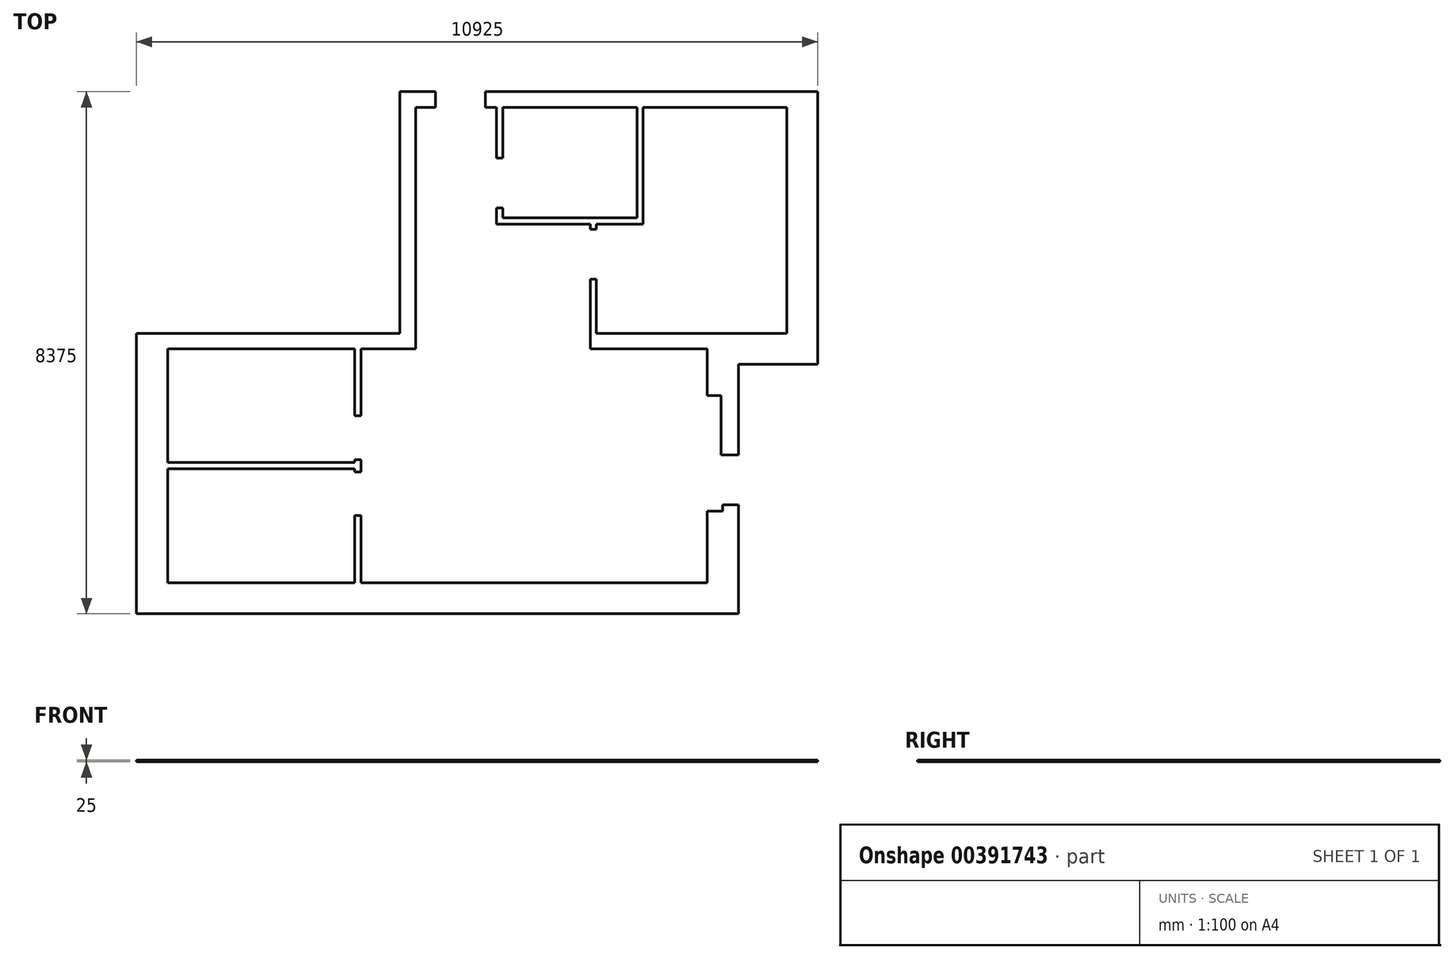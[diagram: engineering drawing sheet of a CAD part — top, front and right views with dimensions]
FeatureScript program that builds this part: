
annotation { "Feature Type Name" : "Feature", "Feature Type Description" : "" }
export const myFeature = defineFeature(function(context is Context, id is Id, definition is map)
    precondition{}
    {
        {
            var Q0;
            Q0=qCreatedBy(makeId("Top.planeOp"),FACE);
            var sketch = newSketch(context, id + "F0", { "sketchPlane" : qUnion([Q0])});
            skLineSegment(sketch, "E0.bottom", {"start": v(0, 0) * mm, "end": v(9650, 0) * mm});
            skLineSegment(sketch, "E0.top", {"start": v(4225, 8375) * mm, "end": v(4795, 8375) * mm});
            skLineSegment(sketch, "E0.left", {"start": v(0, 0) * mm, "end": v(0, 4500) * mm});
            skLineSegment(sketch, "E0.right", {"start": v(9650, 0) * mm, "end": v(9650, 1750) * mm});
            skLineSegment(sketch, "E1.bottom", {"start": v(500, 500) * mm, "end": v(3500, 500) * mm});
            skLineSegment(sketch, "E1.top", {"start": v(500, 4250) * mm, "end": v(3500, 4250) * mm});
            skLineSegment(sketch, "E1.left", {"start": v(500, 500) * mm, "end": v(500, 2325) * mm});
            skLineSegment(sketch, "E1.right", {"start": v(3500, 500) * mm, "end": v(3500, 1575) * mm});
            skLineSegment(sketch, "E2.bottom", {"start": v(3600, 4250) * mm, "end": v(4775, 4250) * mm});
            skLineSegment(sketch, "E2.top", {"start": v(3600, 500) * mm, "end": v(9150, 500) * mm});
            skLineSegment(sketch, "E2.left", {"start": v(3600, 4250) * mm, "end": v(3600, 3175) * mm});
            skLineSegment(sketch, "E2.right", {"start": v(9150, 4250) * mm, "end": v(9150, 3500) * mm});
            skLineSegment(sketch, "E3.bottom", {"start": v(10425, 4500) * mm, "end": v(7375, 4500) * mm});
            skLineSegment(sketch, "E3.left", {"start": v(10425, 4500) * mm, "end": v(10425, 8125) * mm});
            skLineSegment(sketch, "E3.right", {"start": v(7375, 4500) * mm, "end": v(7375, 5370) * mm});
            skLineSegment(sketch, "E4.top", {"start": v(4475, 8125) * mm, "end": v(4795, 8125) * mm});
            skLineSegment(sketch, "E4.left", {"start": v(4475, 4500) * mm, "end": v(4475, 8125) * mm});
            skLineSegment(sketch, "E5.bottom", {"start": v(7275, 4500) * mm, "end": v(5575, 4500) * mm});
            skLineSegment(sketch, "E5.top", {"start": v(7275, 6250) * mm, "end": v(5775, 6250) * mm});
            skLineSegment(sketch, "E5.left", {"start": v(7275, 4500) * mm, "end": v(7275, 5370) * mm});
            skLineSegment(sketch, "E6.top", {"start": v(10425, 8125) * mm, "end": v(8125, 8125) * mm});
            skLineSegment(sketch, "E6.right", {"start": v(5875, 6350) * mm, "end": v(5875, 6510) * mm});
            skLineSegment(sketch, "E7.trimOffspring", {"start": v(5775, 6250) * mm, "end": v(5775, 6510) * mm});
            skLineSegment(sketch, "E8", {"start": v(0, 4500) * mm, "end": v(4225, 4500) * mm});
            skLineSegment(sketch, "E9", {"start": v(4225, 4500) * mm, "end": v(4225, 8375) * mm});
            skLineSegment(sketch, "E10", {"start": v(500, 2325) * mm, "end": v(3500, 2325) * mm});
            skLineSegment(sketch, "E11", {"start": v(500, 2425) * mm, "end": v(3500, 2425) * mm});
            skLineSegment(sketch, "E12.trimOffspring", {"start": v(3500, 2425) * mm, "end": v(3500, 2475) * mm});
            skLineSegment(sketch, "E13.trimOffspring", {"start": v(500, 2425) * mm, "end": v(500, 4250) * mm});
            skLineSegment(sketch, "E14", {"start": v(9650, 4000) * mm, "end": v(10925, 4000) * mm});
            skLineSegment(sketch, "E15", {"start": v(10925, 4000) * mm, "end": v(10925, 8375) * mm});
            skLineSegment(sketch, "E16", {"start": v(3500, 2275) * mm, "end": v(3600, 2275) * mm});
            skLineSegment(sketch, "E17", {"start": v(3500, 1575) * mm, "end": v(3600, 1575) * mm});
            skLineSegment(sketch, "E18", {"start": v(3500, 2475) * mm, "end": v(3600, 2475) * mm});
            skLineSegment(sketch, "E19", {"start": v(3500, 3175) * mm, "end": v(3600, 3175) * mm});
            skLineSegment(sketch, "E20.trimOffspring", {"start": v(3500, 2275) * mm, "end": v(3500, 2325) * mm});
            skLineSegment(sketch, "E21.trimOffspring", {"start": v(3600, 1575) * mm, "end": v(3600, 500) * mm});
            skLineSegment(sketch, "E22.trimOffspring", {"start": v(3500, 3175) * mm, "end": v(3500, 4250) * mm});
            skLineSegment(sketch, "E23.trimOffspring", {"start": v(3600, 2475) * mm, "end": v(3600, 2275) * mm});
            skLineSegment(sketch, "E24", {"start": v(5875, 6350) * mm, "end": v(8025, 6350) * mm});
            skLineSegment(sketch, "E25", {"start": v(7375, 6250) * mm, "end": v(8125, 6250) * mm});
            skLineSegment(sketch, "E26", {"start": v(8125, 6250) * mm, "end": v(8125, 8125) * mm});
            skLineSegment(sketch, "E27", {"start": v(8025, 8125) * mm, "end": v(8025, 6350) * mm});
            skLineSegment(sketch, "E28.trimOffspring", {"start": v(10425, 6350) * mm, "end": v(13543.07, 6350) * mm});
            skLineSegment(sketch, "E29.trimOffspring", {"start": v(8025, 8125) * mm, "end": v(5875, 8125) * mm});
            skLineSegment(sketch, "E30", {"start": v(4775, 4500) * mm, "end": v(4775, 4250) * mm});
            skLineSegment(sketch, "E31", {"start": v(5575, 4250) * mm, "end": v(5575, 4500) * mm});
            skLineSegment(sketch, "E32", {"start": v(7275, 5370) * mm, "end": v(7375, 5370) * mm});
            skLineSegment(sketch, "E33", {"start": v(7375, 6170) * mm, "end": v(7275, 6170) * mm});
            skLineSegment(sketch, "E34.trimOffspring", {"start": v(7275, 6170) * mm, "end": v(7275, 6250) * mm});
            skLineSegment(sketch, "E35.trimOffspring", {"start": v(7375, 6170) * mm, "end": v(7375, 6250) * mm});
            skLineSegment(sketch, "E36.trimOffspring", {"start": v(4775, 4500) * mm, "end": v(4475, 4500) * mm});
            skLineSegment(sketch, "E37.trimOffspring", {"start": v(5575, 4250) * mm, "end": v(9150, 4250) * mm});
            skLineSegment(sketch, "E38", {"start": v(4795, 8125) * mm, "end": v(4795, 8375) * mm});
            skLineSegment(sketch, "E39", {"start": v(5595, 8125) * mm, "end": v(5595, 8375) * mm});
            skLineSegment(sketch, "E40", {"start": v(5875, 6510) * mm, "end": v(5775, 6510) * mm});
            skLineSegment(sketch, "E41", {"start": v(5775, 7310) * mm, "end": v(5875, 7310) * mm});
            skLineSegment(sketch, "E42", {"start": v(9650, 1750) * mm, "end": v(9400, 1750) * mm});
            skLineSegment(sketch, "E43", {"start": v(9600, 2550) * mm, "end": v(9375, 2550) * mm});
            skLineSegment(sketch, "E44.trimOffspring", {"start": v(5595, 8375) * mm, "end": v(10925, 8375) * mm});
            skLineSegment(sketch, "E45.trimOffspring", {"start": v(5595, 8125) * mm, "end": v(5775, 8125) * mm});
            skLineSegment(sketch, "E46.trimOffspring", {"start": v(5875, 7310) * mm, "end": v(5875, 8125) * mm});
            skLineSegment(sketch, "E47.trimOffspring", {"start": v(5775, 7310) * mm, "end": v(5775, 8125) * mm});
            skLineSegment(sketch, "E48", {"start": v(9150, 3500) * mm, "end": v(9375, 3500) * mm});
            skLineSegment(sketch, "E49", {"start": v(9375, 3500) * mm, "end": v(9375, 2550) * mm});
            skLineSegment(sketch, "E50", {"start": v(9400, 1750) * mm, "end": v(9400, 1650) * mm});
            skLineSegment(sketch, "E51", {"start": v(9400, 1650) * mm, "end": v(9150, 1650) * mm});
            skLineSegment(sketch, "E52.trimOffspring", {"start": v(9150, 1650) * mm, "end": v(9150, 500) * mm});
            skPoint(sketch, "E53.orphan", {"position": v(9150, 1750) * mm});
            skLineSegment(sketch, "E54", {"start": v(9600, 2550) * mm, "end": v(9650, 2550) * mm});
            skPoint(sketch, "E55.orphan", {"position": v(9150, 2550) * mm});
            skLineSegment(sketch, "E56.trimOffspring", {"start": v(9650, 2550) * mm, "end": v(9650, 4000) * mm});
            skSolve(sketch);
        }
        {
            var Q0;
            Q0 = qSketchRegion(id + "F0", true);
            extrude(context, id + "F1", {"entities" : qUnion([Q0]), "depth" : 25 * mm});
        }
        {
            var Q0;
            Q0=makeQuery(id+"F1.opExtrude","CAP_FACE",FACE,{"disambiguationData":[OSD([sQuery(id+"F0.wireOp",EDGE,"E0.bottom"),sQuery(id+"F0.wireOp",EDGE,"E0.top"),sQuery(id+"F0.wireOp",EDGE,"E0.left"),sQuery(id+"F0.wireOp",EDGE,"E0.right"),sQuery(id+"F0.wireOp",EDGE,"E1.bottom"),sQuery(id+"F0.wireOp",EDGE,"E1.top"),sQuery(id+"F0.wireOp",EDGE,"E1.left"),sQuery(id+"F0.wireOp",EDGE,"E1.right"),sQuery(id+"F0.wireOp",EDGE,"E2.bottom"),sQuery(id+"F0.wireOp",EDGE,"E2.top"),sQuery(id+"F0.wireOp",EDGE,"E2.left"),sQuery(id+"F0.wireOp",EDGE,"E4.top"),sQuery(id+"F0.wireOp",EDGE,"E4.left"),sQuery(id+"F0.wireOp",EDGE,"E8"),sQuery(id+"F0.wireOp",EDGE,"E9"),sQuery(id+"F0.wireOp",EDGE,"E10"),sQuery(id+"F0.wireOp",EDGE,"E11"),sQuery(id+"F0.wireOp",EDGE,"E12.trimOffspring"),sQuery(id+"F0.wireOp",EDGE,"E13.trimOffspring"),sQuery(id+"F0.wireOp",EDGE,"E16"),sQuery(id+"F0.wireOp",EDGE,"E17"),sQuery(id+"F0.wireOp",EDGE,"E18"),sQuery(id+"F0.wireOp",EDGE,"E19"),sQuery(id+"F0.wireOp",EDGE,"E20.trimOffspring"),sQuery(id+"F0.wireOp",EDGE,"E21.trimOffspring"),sQuery(id+"F0.wireOp",EDGE,"E22.trimOffspring"),sQuery(id+"F0.wireOp",EDGE,"E23.trimOffspring"),sQuery(id+"F0.wireOp",EDGE,"E30"),sQuery(id+"F0.wireOp",EDGE,"E36.trimOffspring"),sQuery(id+"F0.wireOp",EDGE,"E38"),sQuery(id+"F0.wireOp",EDGE,"E42"),sQuery(id+"F0.wireOp",EDGE,"E50"),sQuery(id+"F0.wireOp",EDGE,"E51"),sQuery(id+"F0.wireOp",EDGE,"E52.trimOffspring")])],"isStart":false});
            var sketch = newSketch(context, id + "F2", { "sketchPlane" : qUnion([Q0])});
            skPoint(sketch, "E57.oppositeSnap0", {"position": v(4625, 4500) * mm});
            skLineSegment(sketch, "E57.bottom", {"start": v(4475, 4250) * mm, "end": v(7275, 4250) * mm});
            skLineSegment(sketch, "E57.top", {"start": v(4475, 4500) * mm, "end": v(7275, 4500) * mm});
            skLineSegment(sketch, "E57.left", {"start": v(4475, 4250) * mm, "end": v(4475, 4500) * mm});
            skLineSegment(sketch, "E57.right", {"start": v(7275, 4250) * mm, "end": v(7275, 4500) * mm});
            skSolve(sketch);
        }
        {
            var Q0;
            Q0 = qSketchRegion(id + "F2", true);
            extrude(context, id + "F3", {"entities" : qUnion([Q0]), "operationType" : NewBodyOperationType.REMOVE, "oppositeDirection" : true, "depth" : 25 * mm});
        }
    });
